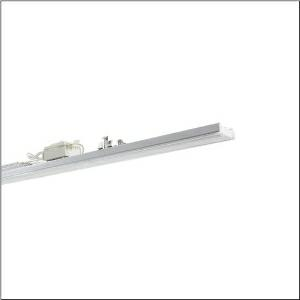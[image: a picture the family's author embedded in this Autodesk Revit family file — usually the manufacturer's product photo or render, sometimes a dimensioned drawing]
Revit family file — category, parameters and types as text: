
# Revit family: licross_r__11_recessed_mo_51tl12dv4fxg3s_b847
name_source: partatom
category: Lighting Fixtures
units: mm (PartAtom-declared; Revit-internal decimal feet)

## family parameters
Cut with Voids When Loaded = No
Host = Face
Light Source = No
Part Type = Normal
Room Calculation Point = No
Round Connector Dimension = Use Diameter
Shared = No

## types (1)
- --- (1 x LED, 1010 lm, 5.5 W, 4000K)
    Apparent Load = 6 VA
    CIE Flux Codes = 67 92 99 100 100
    Color Rendering = 80
    Color Temperature = 4000K
    Default Elevation = 1800 mm
    Description = Licross® 11 Recessed MO, luminaire insert, of sheet steel, coil coated, white, length: 2.250mm, width: 66mm, height: 67mm, LED rated luminous flux: 15.360lm, light colour: 840, control gear: DALI 2 (for two DALI lines), with plug, 6-pole, with phase selection, for trunking rail, 14-core, mains connection: 220..240V, AC, 50/60Hz, rated input power: 88W, for trunking rail, 14-core, internal wiring halogen-free, for emergency light function, converter,control gear: single battery element, battery: LiFePO4, 9Ah, primary optical cover: cover, of PMMA, light emission: direct distribution, primary light characteristic: symmetric, protection rating (complete): IP40, insulation class (complete): insulation class I (protective earthing), certification: CE, UKCA, protection symbol: D if used in an environment without relevant dust loads with corresponding accessories, impact resistance: IK06, permissible ambient temperature for indoor applications: +5..+35°C, standard: EN 60598-2-22, LABS conformity tested according to VDMA 24364:2018-05, reducing of maximum allowable ambient temperature of 5°C with ceiling mounting, corresponds to IFS (International Featured Standards) requirements for safety and quality in the food industry, packaging unit: 1 piece
    Height = 58 mm
    Lamp = 1 x LED
    Lamp Light Flux = 1010 lm
    Lamp Power = 5.5 W
    Lamp count = 1
    Length = 2250 mm
    Luminous efficacy = 184 lm/W
    Manufacturer = Siteco
    ModVariant = No
    Model = 51TL12DV4FXG3S
    Mounting Place = Ceiling
    Mounting Type = Pendant
    Number of Poles = 1
    OnlyDefault = Yes
    Power Factor = 1
    Product Name = Licross® 11 Recessed MO
    Product group = luminaire insert | ceiling pendant
    ProductGroupID = 902
    Protection Class = Protection class I
    Protection Degree = IP 40
    RLX_Detail_Level = 1
    RLX_Emergency_Light_Flux = 0 lm
    RLX_Emergency_Type = 0
    RLX_Emergency_Type_DB = No
    RlxData = <blob elided: 29845 chars, md5=0f6e491d>
    Socket = socket
    Standby Power = 0 W
    System Light Flux = 1010 lm
    System Power = 6 W
    Type Comments = : emergency light operation: 3 h
    Type Image = l_1296930.jpg
    URL = http://relux.com
    VarID = @adj_106801
    Voltage = 0 V
    Weight = 0.00 kg
    Width = 66 mm

## geometry (parser evidence)
native form markers: Blend x4, Sweep x9
no freeform markers — native parametric forms only
